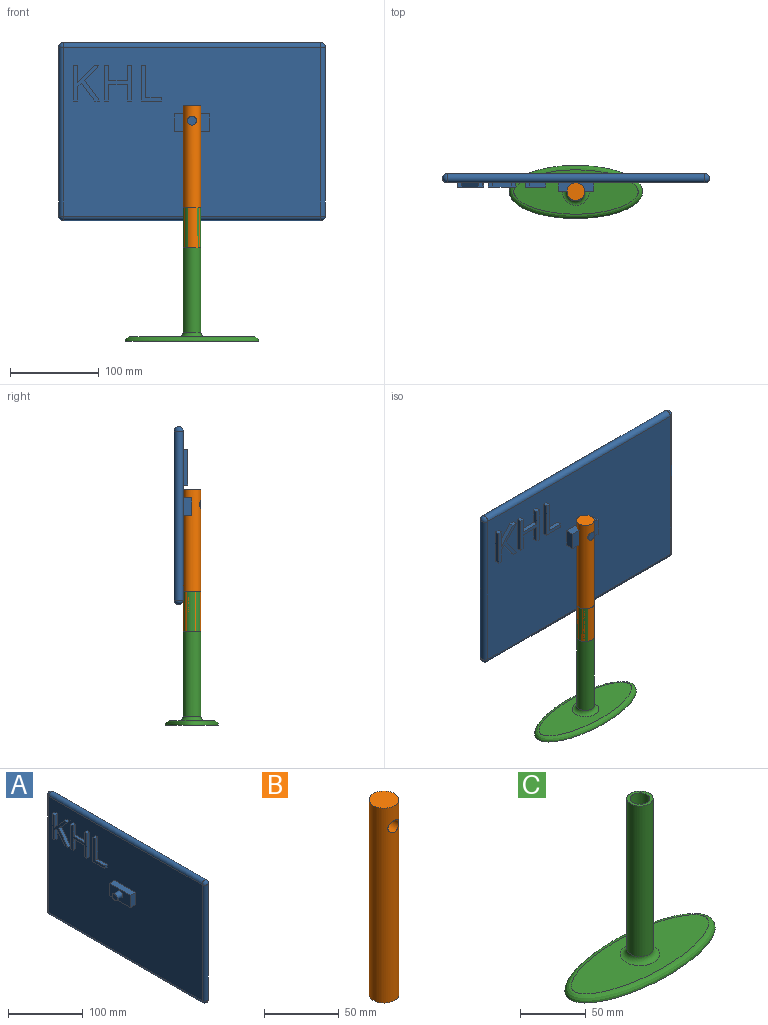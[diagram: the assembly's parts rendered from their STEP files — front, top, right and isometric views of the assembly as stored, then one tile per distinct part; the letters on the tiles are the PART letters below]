
ASSEMBLY  parts=3 mates=2
PART A: 88 faces, bbox 30x300x200 mm
  f0: plane 290x190mm, normal (-1,0,0), area 53135.1mm2, adj f8,f9,f12,f13,f15,f16,f17,f18
  f1: plane 290x190mm, normal (1,0,0), area 4700mm2, adj f2,f3,f4,f5,f8,f9,f12,f13
  f2: plane 180x8mm, normal (0,1,0), area 1440mm2, adj f1,f3,f5,f6
  f3: plane 280x8mm, normal (0,0,1), area 2240mm2, adj f1,f2,f4,f6
  f4: plane 180x8mm, normal (0,-1,0), area 1440mm2, adj f1,f3,f5,f6
  f5: plane 280x8mm, normal (0,0,-1), area 2240mm2, adj f1,f2,f4,f6
  f6: plane 280x180mm, normal (1,0,0), area 48658.3mm2, adj f2,f3,f4,f5,f55,f56,f57,f58
  f7: sphere r=5mm, area 78.5mm2, adj f8,f9
  f8: cylinder r=5mm len=190mm, axis (0,0,-1), area 2984.5mm2, adj f0,f1,f7,f10
  f9: cylinder r=5mm len=290mm, axis (0,-1,0), area 4555.3mm2, adj f0,f1,f7,f11
  f10: sphere r=5mm, area 78.5mm2, adj f8,f12
  f11: sphere r=5mm, area 78.5mm2, adj f9,f13
  f12: cylinder r=5mm len=290mm, axis (0,1,0), area 4555.3mm2, adj f0,f1,f10,f14
  f13: cylinder r=5mm len=190mm, axis (0,0,1), area 2984.5mm2, adj f0,f1,f11,f14
  f14: sphere r=5mm, area 78.5mm2, adj f12,f13
  f15: plane 22.85x16.86mm, normal (0,-0.8,0.59), area 142mm2, adj f0,f16,f26,f27
  f16: plane 17.56x16.25mm, normal (0,-0.73,-0.68), area 119.6mm2, adj f0,f15,f17,f27
  f17: plane 5.55x5mm, normal (0,0,1), area 27.8mm2, adj f0,f16,f18,f27
  f18: plane 20.04x18.32mm, normal (0,0.74,0.67), area 135.8mm2, adj f0,f17,f19,f27
  f19: plane 20.04x5mm, normal (0,-1,0), area 100.2mm2, adj f0,f18,f20,f27
  f20: plane 5x4.7mm, normal (0,0,1), area 23.5mm2, adj f0,f19,f21,f27
  f21: plane 40.41x5mm, normal (0,1,0), area 202mm2, adj f0,f20,f22,f27
  f22: plane 5x4.7mm, normal (0,0,-1), area 23.5mm2, adj f0,f21,f23,f27
  f23: plane 15.84x5mm, normal (0,-1,0), area 79.2mm2, adj f0,f22,f24,f27
  f24: plane 5x4.24mm, normal (0,-0.66,-0.75), area 28.3mm2, adj f0,f23,f25,f27
  f25: plane 19.6x14.73mm, normal (0,0.8,-0.6), area 122.6mm2, adj f0,f24,f26,f27
  f26: plane 5.53x5mm, normal (0,0,-1), area 27.6mm2, adj f0,f15,f25,f27
  f27: plane 40.41x29.19mm, normal (-1,0,0), area 430.4mm2, adj f15,f16,f17,f18,f19,f20,f21,f22
  f28: plane 40.41x5mm, normal (0,-1,0), area 202mm2, adj f0,f29,f39,f40
  f29: plane 5x4.7mm, normal (0,0,1), area 23.5mm2, adj f0,f28,f30,f40
  f30: plane 17.19x5mm, normal (0,1,0), area 86mm2, adj f0,f29,f31,f40
  f31: plane 21.29x5mm, normal (0,0,1), area 106.4mm2, adj f0,f30,f32,f40
  f32: plane 17.19x5mm, normal (0,-1,0), area 86mm2, adj f0,f31,f33,f40
  f33: plane 5x4.7mm, normal (0,0,1), area 23.5mm2, adj f0,f32,f34,f40
  f34: plane 40.41x5mm, normal (0,1,0), area 202mm2, adj f0,f33,f35,f40
  f35: plane 5x4.7mm, normal (0,0,-1), area 23.5mm2, adj f0,f34,f36,f40
  f36: plane 19.01x5mm, normal (0,-1,0), area 95.1mm2, adj f0,f35,f37,f40
  f37: plane 21.29x5mm, normal (0,0,-1), area 106.4mm2, adj f0,f36,f38,f40
  f38: plane 19.01x5mm, normal (0,1,0), area 95.1mm2, adj f0,f37,f39,f40
  f39: plane 5x4.7mm, normal (0,0,-1), area 23.5mm2, adj f0,f28,f38,f40
  f40: plane 40.41x30.68mm, normal (-1,0,0), area 468.9mm2, adj f28,f29,f30,f31,f32,f33,f34,f35
  f41: plane 22.53x5mm, normal (0,0,-1), area 112.6mm2, adj f0,f42,f46,f47
  f42: plane 5x4.25mm, normal (0,-1,0), area 21.3mm2, adj f0,f41,f43,f47
  f43: plane 17.83x5mm, normal (0,0,1), area 89.1mm2, adj f0,f42,f44,f47
  f44: plane 36.15x5mm, normal (0,-1,0), area 180.8mm2, adj f0,f43,f45,f47
  f45: plane 5x4.7mm, normal (0,0,1), area 23.5mm2, adj f0,f44,f46,f47
  f46: plane 40.41x5mm, normal (0,1,0), area 202mm2, adj f0,f41,f45,f47
  f47: plane 40.41x22.53mm, normal (-1,0,0), area 265.6mm2, adj f41,f42,f43,f44,f45,f46
  f48: plane 20x10mm, normal (0,1,0), area 200mm2, adj f0,f49,f51,f52
  f49: plane 40x10mm, normal (0,0,1), area 400mm2, adj f0,f48,f50,f52
  f50: plane 20x10mm, normal (0,-1,0), area 200mm2, adj f0,f49,f51,f52
  f51: plane 40x10mm, normal (0,0,-1), area 400mm2, adj f0,f48,f50,f52
  f52: plane 40x20mm, normal (-1,0,0), area 721.5mm2, adj f48,f49,f50,f51,f53
  f53: cylinder r=5mm len=10mm, axis (1,0,0), area 314.2mm2, adj f52,f54
  f54: plane 10x10mm, normal (-1,0,0), area 78.5mm2, adj f53
  f55: plane 27.94x20.61mm, normal (0,0.8,0.59), area 173.6mm2, adj f6,f56,f66,f67
  f56: plane 21.47x19.86mm, normal (0,0.73,-0.68), area 146.2mm2, adj f6,f55,f57,f67
  f57: plane 6.79x5mm, normal (0,0,1), area 34mm2, adj f6,f56,f58,f67
  f58: plane 24.5x22.41mm, normal (0,-0.74,0.67), area 166mm2, adj f6,f57,f59,f67
  f59: plane 24.5x5mm, normal (0,1,0), area 122.5mm2, adj f6,f58,f60,f67
  f60: plane 5.74x5mm, normal (0,0,1), area 28.7mm2, adj f6,f59,f61,f67
  f61: plane 49.41x5mm, normal (0,-1,0), area 247mm2, adj f6,f60,f62,f67
  f62: plane 5.74x5mm, normal (0,0,-1), area 28.7mm2, adj f6,f61,f63,f67
  f63: plane 19.37x5mm, normal (0,1,0), area 96.8mm2, adj f6,f62,f64,f67
  f64: plane 5.18x5mm, normal (0,0.66,-0.75), area 34.6mm2, adj f6,f63,f65,f67
  f65: plane 23.96x18mm, normal (0,-0.8,-0.6), area 149.9mm2, adj f6,f64,f66,f67
  f66: plane 6.76x5mm, normal (0,0,-1), area 33.8mm2, adj f6,f55,f65,f67
  f67: plane 49.41x35.69mm, normal (1,0,0), area 643.5mm2, adj f55,f56,f57,f58,f59,f60,f61,f62
  f68: plane 49.41x5mm, normal (0,1,0), area 247mm2, adj f6,f69,f79,f80
  f69: plane 5.74x5mm, normal (0,0,1), area 28.7mm2, adj f6,f68,f70,f80
  f70: plane 21.02x5mm, normal (0,-1,0), area 105.1mm2, adj f6,f69,f71,f80
  f71: plane 26.03x5mm, normal (0,0,1), area 130.1mm2, adj f6,f70,f72,f80
  f72: plane 21.02x5mm, normal (0,1,0), area 105.1mm2, adj f6,f71,f73,f80
  f73: plane 5.74x5mm, normal (0,0,1), area 28.7mm2, adj f6,f72,f74,f80
  f74: plane 49.41x5mm, normal (0,-1,0), area 247mm2, adj f6,f73,f75,f80
  f75: plane 5.74x5mm, normal (0,0,-1), area 28.7mm2, adj f6,f74,f76,f80
  f76: plane 23.25x5mm, normal (0,1,0), area 116.2mm2, adj f6,f75,f77,f80
  f77: plane 26.03x5mm, normal (0,0,-1), area 130.1mm2, adj f6,f76,f78,f80
  f78: plane 23.25x5mm, normal (0,-1,0), area 116.2mm2, adj f6,f77,f79,f80
  f79: plane 5.74x5mm, normal (0,0,-1), area 28.7mm2, adj f6,f68,f78,f80
  f80: plane 49.41x37.51mm, normal (1,0,0), area 701.1mm2, adj f68,f69,f70,f71,f72,f73,f74,f75
  f81: plane 27.54x5mm, normal (0,0,-1), area 137.7mm2, adj f6,f82,f86,f87
  f82: plane 5.2x5mm, normal (0,1,0), area 26mm2, adj f6,f81,f83,f87
  f83: plane 21.8x5mm, normal (0,0,1), area 109mm2, adj f6,f82,f84,f87
  f84: plane 44.21x5mm, normal (0,1,0), area 221mm2, adj f6,f83,f85,f87
  f85: plane 5.74x5mm, normal (0,0,1), area 28.7mm2, adj f6,f84,f86,f87
  f86: plane 49.41x5mm, normal (0,-1,0), area 247mm2, adj f6,f81,f85,f87
  f87: plane 49.41x27.54mm, normal (1,0,0), area 397.1mm2, adj f81,f82,f83,f84,f85,f86
PART B: 5 faces, bbox 20x20x160 mm
  f0: cylinder r=10mm len=160mm, axis (0,0,1), area 9971.7mm2, adj f1,f2,f3
  f1: plane 20x20mm, normal (0,0,-1), area 314.2mm2, adj f0
  f2: plane 20x20mm, normal (0,0,1), area 314.2mm2, adj f0
  f3: cylinder r=5mm len=10mm, axis (0,-1,0), area 293.5mm2, adj f0,f4
  f4: plane 10x10mm, normal (0,-1,0), area 78.5mm2, adj f3
PART C: 8 faces, bbox 150.1x60.1x150.1 mm
  f0: cylinder r=10mm len=140mm, axis (0,0,-1), area 8796.5mm2, adj f1,f6
  f1: plane 20x20mm, normal (0,0,1), area 137.4mm2, adj f0,f2
  f2: cylinder r=7.5mm len=145mm, axis (0,0,-1), area 6833mm2, adj f1,f3
  f3: plane 15x15mm, normal (0,0,1), area 176.7mm2, adj f2
  f4: plane 140x50.01mm, normal (0,0,1), area 4714.9mm2, adj f6,f7
  f5: plane 150.08x60.08mm, normal (0,0,-1), area 7068.6mm2, adj f7
  f6: torus R=15mm, axis (0,0,1), area 583.1mm2, adj f0,f4
  f7: bspline ~150.01x60.01mm, area 2623.4mm2, adj f4,f5
PLACE A rot(axis=(0,0,1),90deg) t=(-723.41,200.93,177.64)mm
PLACE B rot(axis=(0.7,0.47,-0.53),0deg) t=(-723.41,190.93,206.8)mm
PLACE C rot(axis=(0.7,0.47,-0.53),0deg) t=(-723.41,190.93,-58.2)mm
MATE revolute A.f53 <-> B.f3  axis (0,-1,0) through (-723.41,190.93,189.95)mm
MATE slider C.f0 <-> B.f0  axis (0,0,1) through (-723.41,190.93,-53.2)mm
